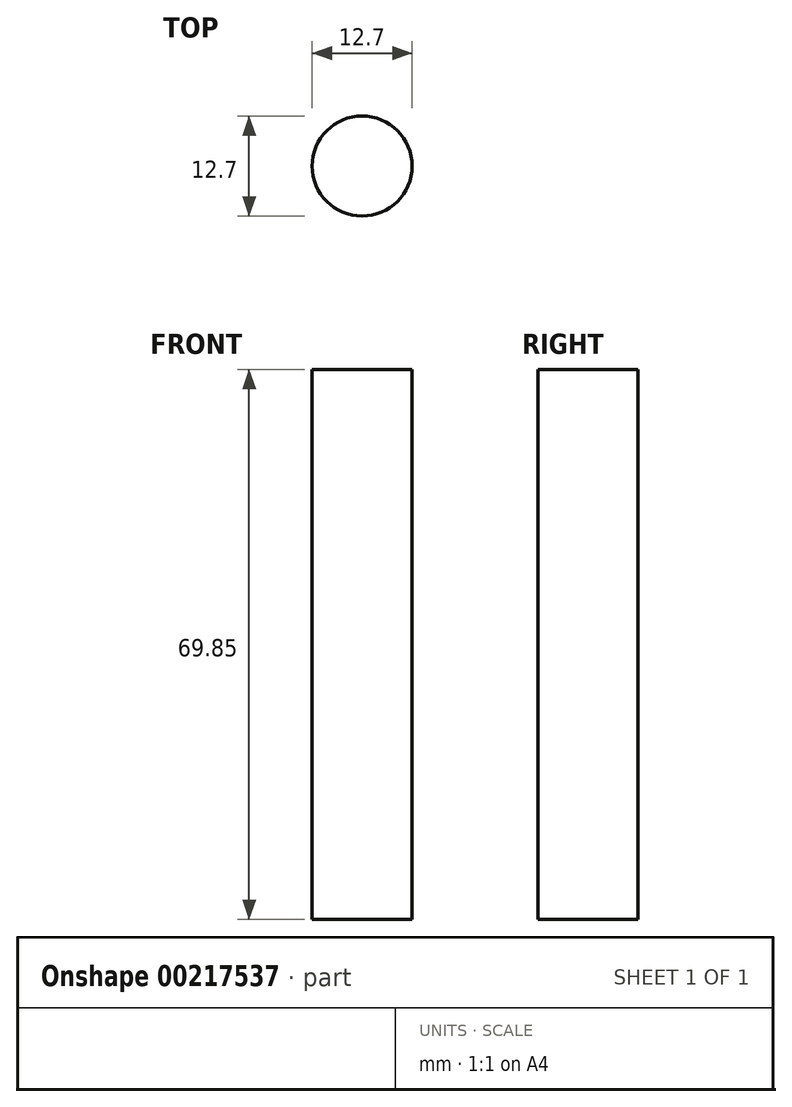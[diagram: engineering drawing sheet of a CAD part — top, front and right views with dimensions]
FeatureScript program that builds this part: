
annotation { "Feature Type Name" : "Feature", "Feature Type Description" : "" }
export const myFeature = defineFeature(function(context is Context, id is Id, definition is map)
    precondition{}
    {
        {
            var Q0;
            Q0=qCreatedBy(makeId("Top.planeOp"),FACE);
            var sketch = newSketch(context, id + "F0", { "sketchPlane" : qUnion([Q0])});
            skCircle(sketch, "E0", {"center": v(0, 0) * mm, "radius": 6.35 * mm});
            skSolve(sketch);
        }
        {
            var Q0;
            Q0 = qSketchRegion(id + "F0", true);
            extrude(context, id + "F1", {"entities" : qUnion([Q0]), "depth" : 69.85 * mm});
        }
    });
